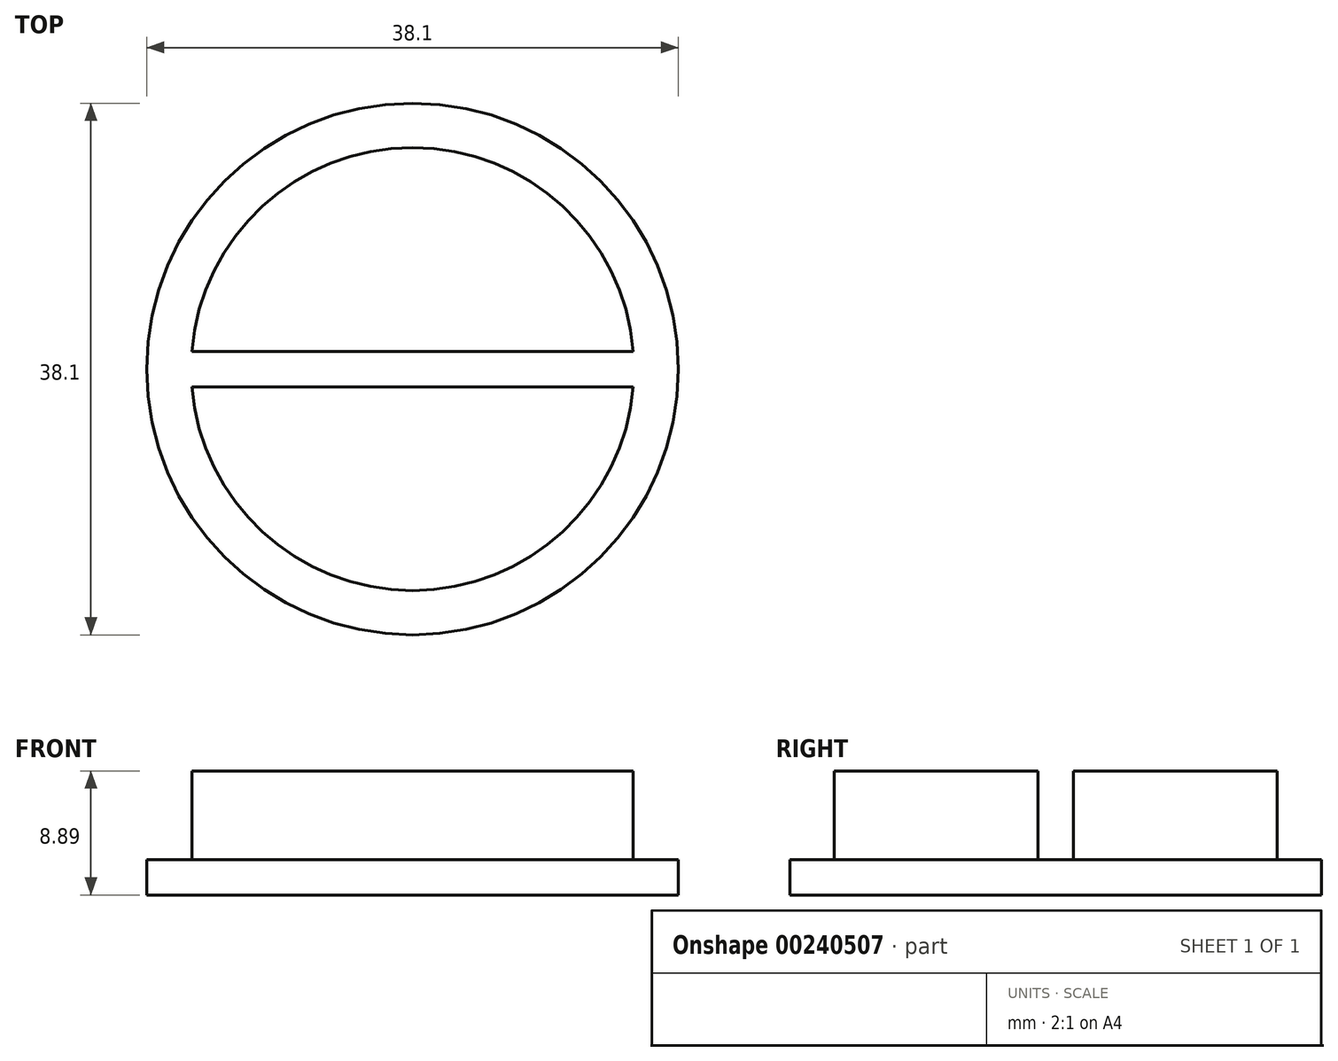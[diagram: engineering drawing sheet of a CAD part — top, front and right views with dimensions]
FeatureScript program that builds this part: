
annotation { "Feature Type Name" : "Feature", "Feature Type Description" : "" }
export const myFeature = defineFeature(function(context is Context, id is Id, definition is map)
    precondition{}
    {
        {
            var Q0;
            Q0=qCreatedBy(makeId("Top.planeOp"),FACE);
            var sketch = newSketch(context, id + "F0", { "sketchPlane" : qUnion([Q0])});
            skCircle(sketch, "E0", {"center": v(0, 0) * mm, "radius": 19.05 * mm});
            skSolve(sketch);
        }
        {
            var Q0;
            Q0 = qSketchRegion(id + "F0", true);
            extrude(context, id + "F1", {"entities" : qUnion([Q0]), "depth" : 2.54 * mm});
        }
        {
            var Q0;
            Q0=makeQuery(id+"F1.opExtrude","CAP_FACE",FACE,{"disambiguationData":[OSD([sQuery(id+"F0.wireOp",EDGE,"E0")])],"isStart":false});
            var sketch = newSketch(context, id + "F2", { "sketchPlane" : qUnion([Q0])});
            skArc(sketch, "E1", {"start": v(-15.82, 1.27) * mm, "mid": v(-15.87, 0) * mm, "end": v(-15.82, -1.27) * mm, "construction": true});
            skArc(sketch, "E2", {"start": v(-15.82, -1.27) * mm, "mid": v(0, -15.87) * mm, "end": v(15.82, -1.27) * mm});
            skArc(sketch, "E3", {"start": v(15.82, -1.27) * mm, "mid": v(15.87, 0) * mm, "end": v(15.82, 1.27) * mm, "construction": true});
            skArc(sketch, "E4", {"start": v(15.82, 1.27) * mm, "mid": v(0, 15.87) * mm, "end": v(-15.82, 1.27) * mm});
            skLineSegment(sketch, "E5", {"start": v(15.82, 1.27) * mm, "end": v(-15.82, 1.27) * mm});
            skLineSegment(sketch, "E6", {"start": v(-15.82, -1.27) * mm, "end": v(15.82, -1.27) * mm});
            skSolve(sketch);
        }
        {
            var Q0;
            Q0 = qSketchRegion(id + "F2", true);
            extrude(context, id + "F3", {"entities" : qUnion([Q0]), "operationType" : NewBodyOperationType.ADD, "depth" : 6.35 * mm});
        }
    });
